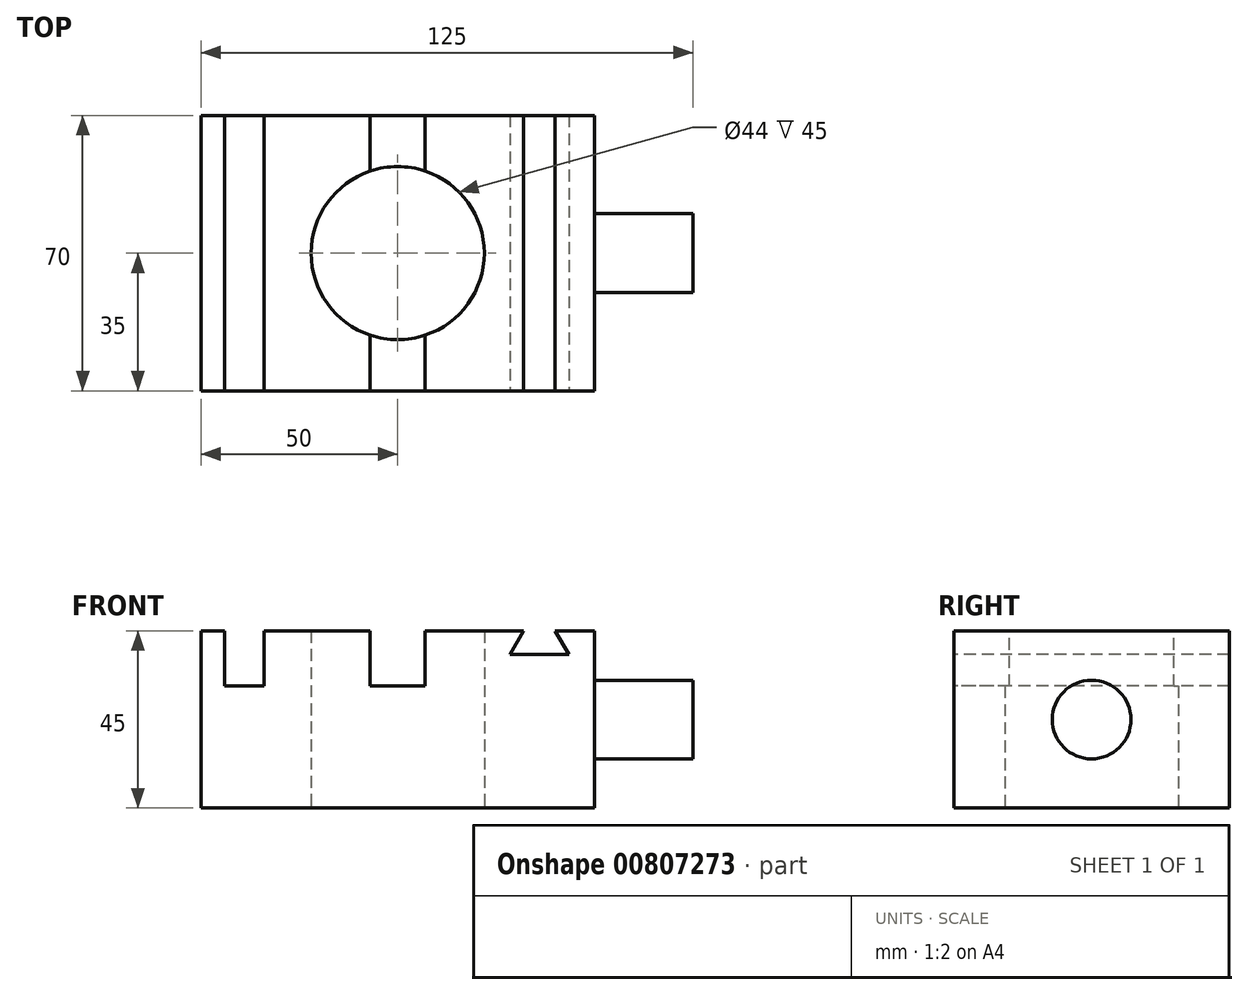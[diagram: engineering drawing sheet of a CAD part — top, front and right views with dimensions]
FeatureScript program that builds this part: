
annotation { "Feature Type Name" : "Feature", "Feature Type Description" : "" }
export const myFeature = defineFeature(function(context is Context, id is Id, definition is map)
    precondition{}
    {
        {
            var Q0;
            Q0=qCreatedBy(makeId("Top.planeOp"),FACE);
            var sketch = newSketch(context, id + "F0", { "sketchPlane" : qUnion([Q0])});
            skLineSegment(sketch, "E0.bottom", {"start": v(50, -35) * mm, "end": v(-50, -35) * mm});
            skLineSegment(sketch, "E0.top", {"start": v(50, 35) * mm, "end": v(-50, 35) * mm});
            skLineSegment(sketch, "E0.left", {"start": v(50, -35) * mm, "end": v(50, 35) * mm});
            skLineSegment(sketch, "E0.right", {"start": v(-50, -35) * mm, "end": v(-50, 35) * mm});
            skPoint(sketch, "E0.middle", {"position": v(0, 0) * mm});
            skCircle(sketch, "E1", {"center": v(0, 0) * mm, "radius": 22 * mm});
            skSolve(sketch);
        }
        {
            var Q0;
            Q0 = qSketchRegion(id + "F0", true);
            extrude(context, id + "F1", {"entities" : qUnion([Q0]), "depth" : 45 * mm, "offsetDistance" : 25 * mm});
        }
        {
            var Q0;
            Q0=makeQuery(id+"F1.opExtrude","CAP_FACE",FACE,{"disambiguationData":[OSD([sQuery(id+"F0.wireOp",EDGE,"E0.bottom"),sQuery(id+"F0.wireOp",EDGE,"E0.top"),sQuery(id+"F0.wireOp",EDGE,"E0.left"),sQuery(id+"F0.wireOp",EDGE,"E0.right")])],"isStart":false});
            var sketch = newSketch(context, id + "F2", { "sketchPlane" : qUnion([Q0])});
            skLineSegment(sketch, "E2", {"start": v(-44, 35) * mm, "end": v(-44, -35) * mm});
            skLineSegment(sketch, "E3", {"start": v(-44, -35) * mm, "end": v(-34, -35) * mm});
            skLineSegment(sketch, "E4", {"start": v(-34, -35) * mm, "end": v(-34, 35) * mm});
            skLineSegment(sketch, "E5", {"start": v(-34, 35) * mm, "end": v(-44, 35) * mm});
            skCircle(sketch, "E6", {"center": v(0, 0) * mm, "radius": 20 * mm});
            skLineSegment(sketch, "E7.bottom", {"start": v(-7, 35) * mm, "end": v(7, 35) * mm});
            skLineSegment(sketch, "E7.top", {"start": v(-7, -35) * mm, "end": v(7, -35) * mm});
            skLineSegment(sketch, "E7.left", {"start": v(-7, 35) * mm, "end": v(-7, -35) * mm});
            skLineSegment(sketch, "E7.right", {"start": v(7, 35) * mm, "end": v(7, -35) * mm});
            skLineSegment(sketch, "E8", {"start": v(0, 35) * mm, "end": v(0, -35) * mm, "construction": true});
            skSolve(sketch);
        }
        {
            var Q0;
            Q0=makeQuery(id+"F2.imprint","IMPRINT",FACE,{"disambiguationData":[TD([[makeQuery(id+"F2.imprint","IMPRINT",EDGE,{"derivedFrom":sQuery(id+"F2.wireOp",EDGE,"E2")}),1.0]])]});
            var Q1;
            {var subQ0=sQuery(id+"F2.wireOp",EDGE,"E7.top");Q1=makeQuery(id+"F2.imprint","IMPRINT",FACE,{"disambiguationData":[TD([[makeQuery(id+"F2.imprint","IMPRINT",EDGE,{"derivedFrom":subQ0}),-1.0]])]});}
            var Q2;
            {var subQ0=sQuery(id+"F2.wireOp",EDGE,"E7.bottom");Q2=makeQuery(id+"F2.imprint","IMPRINT",FACE,{"disambiguationData":[TD([[makeQuery(id+"F2.imprint","IMPRINT",EDGE,{"derivedFrom":subQ0}),1.0]])]});}
            extrude(context, id + "F3", {"entities" : qUnion([Q0, Q1, Q2]), "operationType" : NewBodyOperationType.REMOVE, "oppositeDirection" : true, "depth" : 14 * mm, "offsetDistance" : 25 * mm});
        }
        {
            var Q0;
            Q0=makeQuery(id+"F1.opExtrude","SWEPT_FACE",FACE,{"disambiguationData":[OSD([sQuery(id+"F0.wireOp",EDGE,"E0.bottom")])]});
            var sketch = newSketch(context, id + "F4", { "sketchPlane" : qUnion([Q0])});
            skLineSegment(sketch, "E9", {"start": v(32, 45) * mm, "end": v(28.54, 39) * mm});
            skLineSegment(sketch, "E10", {"start": v(28.54, 39) * mm, "end": v(43.46, 39) * mm});
            skLineSegment(sketch, "E11", {"start": v(43.46, 39) * mm, "end": v(40, 45) * mm});
            skLineSegment(sketch, "E12", {"start": v(40, 45) * mm, "end": v(32, 45) * mm});
            skLineSegment(sketch, "E13", {"start": v(36, 39) * mm, "end": v(36, 45) * mm, "construction": true});
            skSolve(sketch);
        }
        {
            var Q0;
            Q0=makeQuery(id+"F4.imprint","IMPRINT",FACE,{"disambiguationData":[TD([[makeQuery(id+"F4.imprint","IMPRINT",EDGE,{"derivedFrom":sQuery(id+"F4.wireOp",EDGE,"E9")}),1.0]])]});
            extrude(context, id + "F5", {"entities" : qUnion([Q0]), "operationType" : NewBodyOperationType.REMOVE, "endBound" : BoundingType.THROUGH_ALL, "oppositeDirection" : true, "depth" : 25 * mm, "offsetDistance" : 25 * mm});
        }
        {
            var Q0;
            Q0=makeQuery(id+"F1.opExtrude","SWEPT_FACE",FACE,{"disambiguationData":[OSD([sQuery(id+"F0.wireOp",EDGE,"E0.left")])]});
            var sketch = newSketch(context, id + "F6", { "sketchPlane" : qUnion([Q0])});
            skCircle(sketch, "E14", {"center": v(0, 22.5) * mm, "radius": 10 * mm});
            skPoint(sketch, "E14.centerSnap0", {"position": v(-35, 22.5) * mm});
            skPoint(sketch, "E14.centerSnap1", {"position": v(0, 45) * mm});
            skSolve(sketch);
        }
        {
            var Q0;
            Q0=makeQuery(id+"F6.imprint","IMPRINT",FACE,{"disambiguationData":[TD([[makeQuery(id+"F6.imprint","IMPRINT",EDGE,{"derivedFrom":sQuery(id+"F6.wireOp",EDGE,"E14")}),1.0]])]});
            extrude(context, id + "F7", {"entities" : qUnion([Q0]), "operationType" : NewBodyOperationType.ADD, "depth" : 25 * mm, "offsetDistance" : 25 * mm});
        }
    });
